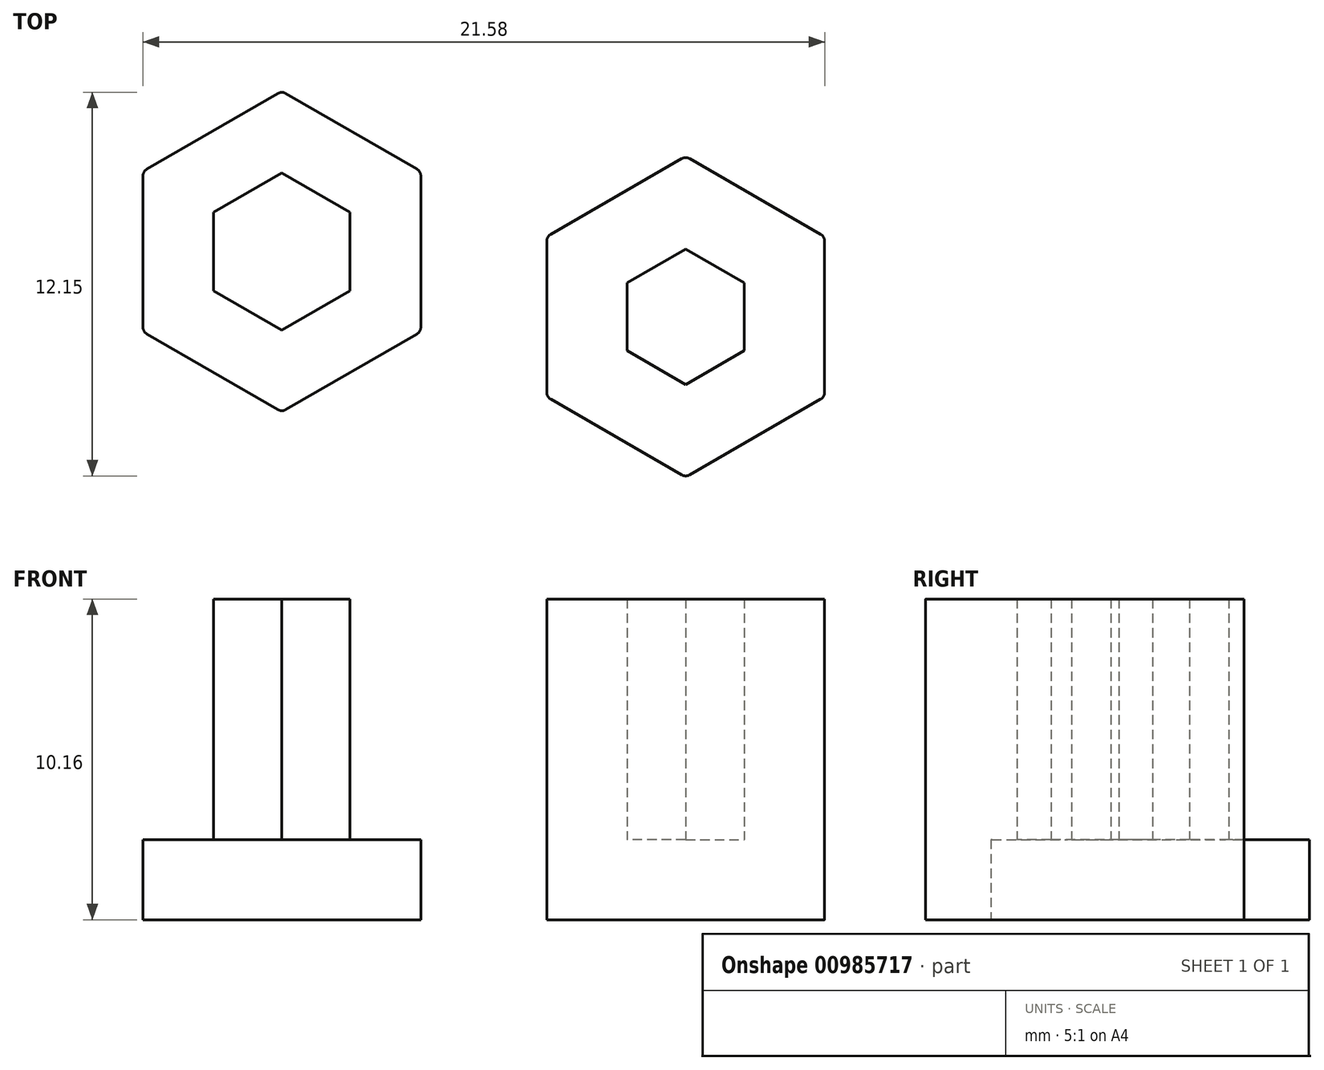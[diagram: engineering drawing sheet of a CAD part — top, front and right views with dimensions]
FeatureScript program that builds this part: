
annotation { "Feature Type Name" : "Feature", "Feature Type Description" : "" }
export const myFeature = defineFeature(function(context is Context, id is Id, definition is map)
    precondition{}
    {
        {
            var Q0;
            Q0=qCreatedBy(makeId("Top.planeOp"),FACE);
            var sketch = newSketch(context, id + "F0", { "sketchPlane" : qUnion([Q0])});
            skCircle(sketch, "E0.cCircle", {"center": v(0, 0) * mm, "radius": 1.86 * mm, "construction": true});
            skLineSegment(sketch, "E0.0", {"start": v(1.86, 1.07) * mm, "end": v(1.86, -1.07) * mm});
            skLineSegment(sketch, "E0.1", {"start": v(1.86, -1.07) * mm, "end": v(0, -2.15) * mm});
            skLineSegment(sketch, "E0.2", {"start": v(0, -2.15) * mm, "end": v(-1.86, -1.07) * mm});
            skLineSegment(sketch, "E0.3", {"start": v(-1.86, -1.07) * mm, "end": v(-1.86, 1.07) * mm});
            skLineSegment(sketch, "E0.4", {"start": v(-1.86, 1.07) * mm, "end": v(0, 2.15) * mm});
            skLineSegment(sketch, "E0.5", {"start": v(0, 2.15) * mm, "end": v(1.86, 1.07) * mm});
            skPoint(sketch, "E0.0.midPoint", {"position": v(1.86, 0) * mm});
            skLineSegment(sketch, "E1.0", {"start": v(-4.27, 2.61) * mm, "end": v(-0.13, 5) * mm});
            skLineSegment(sketch, "E1.1", {"start": v(4.4, 2.4) * mm, "end": v(4.4, -2.4) * mm});
            skLineSegment(sketch, "E1.2", {"start": v(4.27, -2.61) * mm, "end": v(0.13, -5) * mm});
            skLineSegment(sketch, "E1.3", {"start": v(0.13, 5) * mm, "end": v(4.27, 2.61) * mm});
            skLineSegment(sketch, "E1.4", {"start": v(-0.13, -5) * mm, "end": v(-4.27, -2.61) * mm});
            skLineSegment(sketch, "E1.5", {"start": v(-4.4, -2.4) * mm, "end": v(-4.4, 2.4) * mm});
            skPoint(sketch, "E2.visualSharp", {"position": v(4.4, 2.54) * mm});
            skArc(sketch, "E2.filletArc", {"start": v(4.4, 2.4) * mm, "mid": v(4.37, 2.52) * mm, "end": v(4.27, 2.61) * mm});
            skPoint(sketch, "E3.visualSharp", {"position": v(0, 5.08) * mm});
            skArc(sketch, "E3.filletArc", {"start": v(0.13, 5) * mm, "mid": v(0, 5.04) * mm, "end": v(-0.13, 5) * mm});
            skPoint(sketch, "E4.visualSharp", {"position": v(-4.4, 2.54) * mm});
            skArc(sketch, "E4.filletArc", {"start": v(-4.27, 2.61) * mm, "mid": v(-4.37, 2.52) * mm, "end": v(-4.4, 2.4) * mm});
            skPoint(sketch, "E5.visualSharp", {"position": v(-4.4, -2.54) * mm});
            skArc(sketch, "E5.filletArc", {"start": v(-4.4, -2.4) * mm, "mid": v(-4.37, -2.52) * mm, "end": v(-4.27, -2.61) * mm});
            skPoint(sketch, "E6.visualSharp", {"position": v(0, -5.08) * mm});
            skArc(sketch, "E6.filletArc", {"start": v(-0.13, -5) * mm, "mid": v(0, -5.04) * mm, "end": v(0.13, -5) * mm});
            skPoint(sketch, "E7.visualSharp", {"position": v(4.4, -2.54) * mm});
            skArc(sketch, "E7.filletArc", {"start": v(4.27, -2.61) * mm, "mid": v(4.37, -2.52) * mm, "end": v(4.4, -2.4) * mm});
            skCircle(sketch, "E8.cCircle", {"center": v(-12.78, 2.07) * mm, "radius": 2.16 * mm, "construction": true});
            skLineSegment(sketch, "E8.0", {"start": v(-10.63, 3.31) * mm, "end": v(-10.63, 0.82) * mm});
            skLineSegment(sketch, "E8.1", {"start": v(-10.63, 0.82) * mm, "end": v(-12.78, -0.43) * mm});
            skLineSegment(sketch, "E8.2", {"start": v(-12.78, -0.43) * mm, "end": v(-14.94, 0.82) * mm});
            skLineSegment(sketch, "E8.3", {"start": v(-14.94, 0.82) * mm, "end": v(-14.94, 3.31) * mm});
            skLineSegment(sketch, "E8.4", {"start": v(-14.94, 3.31) * mm, "end": v(-12.78, 4.56) * mm});
            skLineSegment(sketch, "E8.5", {"start": v(-12.78, 4.56) * mm, "end": v(-10.63, 3.31) * mm});
            skPoint(sketch, "E8.0.midPoint", {"position": v(-10.63, 2.07) * mm});
            skLineSegment(sketch, "E9.0", {"start": v(-17.06, 4.68) * mm, "end": v(-12.91, 7.07) * mm});
            skLineSegment(sketch, "E9.1", {"start": v(-8.38, 4.46) * mm, "end": v(-8.38, -0.33) * mm});
            skLineSegment(sketch, "E9.2", {"start": v(-8.51, -0.55) * mm, "end": v(-12.66, -2.94) * mm});
            skLineSegment(sketch, "E9.3", {"start": v(-12.66, 7.07) * mm, "end": v(-8.51, 4.68) * mm});
            skLineSegment(sketch, "E9.4", {"start": v(-12.91, -2.94) * mm, "end": v(-17.06, -0.55) * mm});
            skLineSegment(sketch, "E9.5", {"start": v(-17.18, -0.33) * mm, "end": v(-17.18, 4.46) * mm});
            skPoint(sketch, "E10.visualSharp", {"position": v(-8.38, 4.6) * mm});
            skArc(sketch, "E10.filletArc", {"start": v(-8.38, 4.46) * mm, "mid": v(-8.42, 4.59) * mm, "end": v(-8.51, 4.68) * mm});
            skPoint(sketch, "E11.visualSharp", {"position": v(-12.78, 7.15) * mm});
            skArc(sketch, "E11.filletArc", {"start": v(-12.66, 7.07) * mm, "mid": v(-12.78, 7.1) * mm, "end": v(-12.91, 7.07) * mm});
            skPoint(sketch, "E12.visualSharp", {"position": v(-17.18, 4.6) * mm});
            skArc(sketch, "E12.filletArc", {"start": v(-17.06, 4.68) * mm, "mid": v(-17.15, 4.59) * mm, "end": v(-17.18, 4.46) * mm});
            skPoint(sketch, "E13.visualSharp", {"position": v(-17.18, -0.47) * mm});
            skArc(sketch, "E13.filletArc", {"start": v(-17.18, -0.33) * mm, "mid": v(-17.15, -0.45) * mm, "end": v(-17.06, -0.55) * mm});
            skPoint(sketch, "E14.visualSharp", {"position": v(-12.78, -3.01) * mm});
            skArc(sketch, "E14.filletArc", {"start": v(-12.91, -2.94) * mm, "mid": v(-12.78, -2.97) * mm, "end": v(-12.66, -2.94) * mm});
            skPoint(sketch, "E15.visualSharp", {"position": v(-8.38, -0.47) * mm});
            skArc(sketch, "E15.filletArc", {"start": v(-8.51, -0.55) * mm, "mid": v(-8.42, -0.45) * mm, "end": v(-8.38, -0.33) * mm});
            skSolve(sketch);
        }
        {
            var Q0;
            Q0=makeQuery(id+"F0.imprint","IMPRINT",FACE,{"disambiguationData":[TD([[makeQuery(id+"F0.imprint","IMPRINT",EDGE,{"derivedFrom":sQuery(id+"F0.wireOp",EDGE,"E8.0")}),-1.0]])]});
            extrude(context, id + "F1", {"entities" : qUnion([Q0]), "depth" : 10.16 * mm, "offsetDistance" : 25.4 * mm});
        }
        {
            var Q0;
            Q0=makeQuery(id+"F0.imprint","IMPRINT",FACE,{"disambiguationData":[TD([[makeQuery(id+"F0.imprint","IMPRINT",EDGE,{"derivedFrom":sQuery(id+"F0.wireOp",EDGE,"E8.0")}),1.0]])]});
            extrude(context, id + "F2", {"entities" : qUnion([Q0]), "operationType" : NewBodyOperationType.ADD, "depth" : 2.54 * mm, "offsetDistance" : 25.4 * mm});
        }
        {
            var Q0;
            Q0=makeQuery(id+"F0.imprint","IMPRINT",FACE,{"disambiguationData":[TD([[makeQuery(id+"F0.imprint","IMPRINT",EDGE,{"derivedFrom":sQuery(id+"F0.wireOp",EDGE,"E0.0")}),1.0]])]});
            extrude(context, id + "F3", {"entities" : qUnion([Q0]), "depth" : 10.16 * mm, "offsetDistance" : 25.4 * mm});
        }
        {
            var Q0;
            Q0=makeQuery(id+"F0.imprint","IMPRINT",FACE,{"disambiguationData":[TD([[makeQuery(id+"F0.imprint","IMPRINT",EDGE,{"derivedFrom":sQuery(id+"F0.wireOp",EDGE,"E0.0")}),-1.0]])]});
            extrude(context, id + "F4", {"entities" : qUnion([Q0]), "operationType" : NewBodyOperationType.ADD, "depth" : 2.54 * mm, "offsetDistance" : 25.4 * mm});
        }
    });
